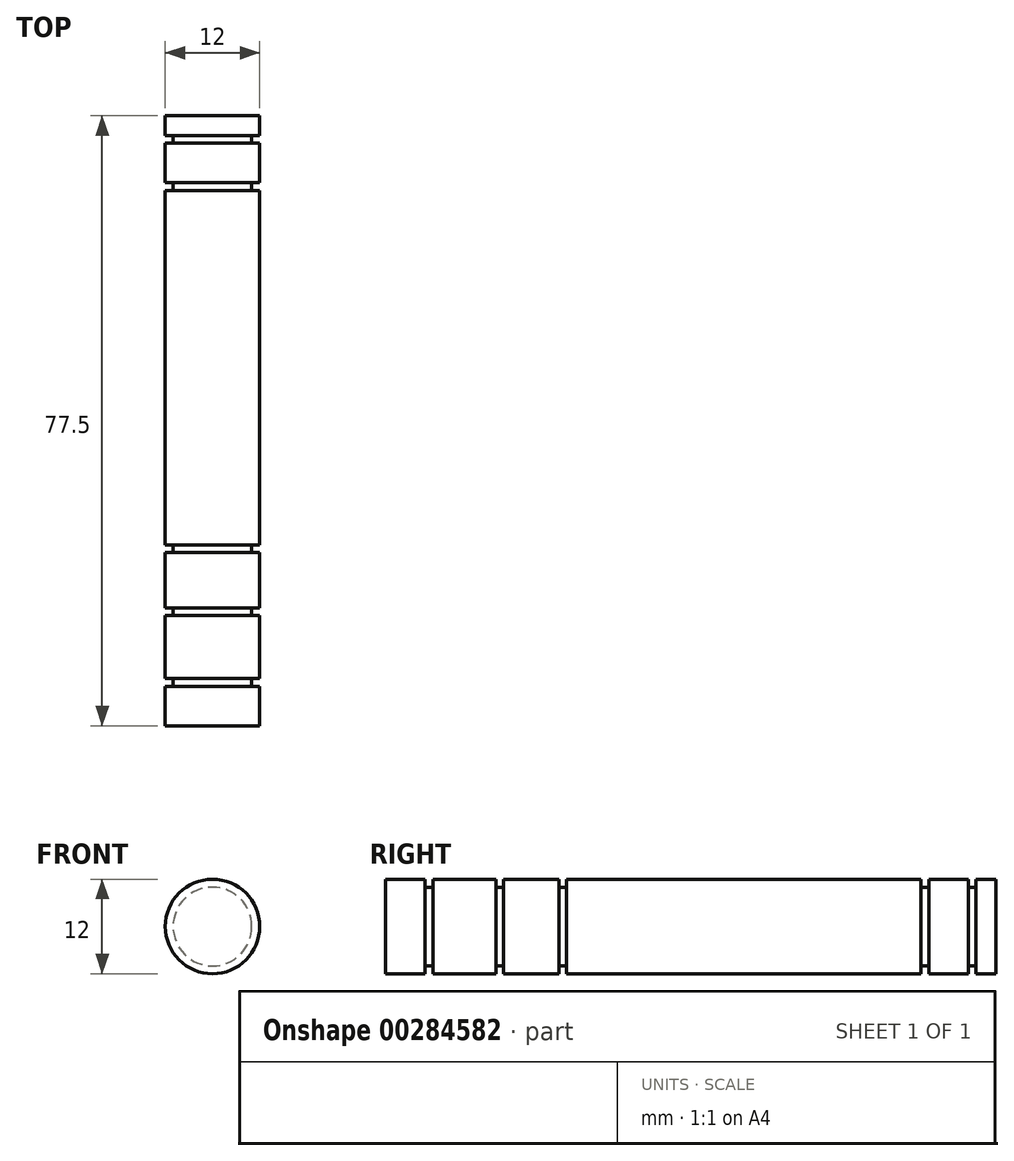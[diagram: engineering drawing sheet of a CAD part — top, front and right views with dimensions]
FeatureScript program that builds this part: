
annotation { "Feature Type Name" : "Feature", "Feature Type Description" : "" }
export const myFeature = defineFeature(function(context is Context, id is Id, definition is map)
    precondition{}
    {
        {
            var Q0;
            Q0=qCreatedBy(makeId("Right.planeOp"),FACE);
            var sketch = newSketch(context, id + "F0", { "sketchPlane" : qUnion([Q0])});
            skLineSegment(sketch, "E0.top", {"start": v(0, 6) * mm, "end": v(2, 6) * mm});
            skLineSegment(sketch, "E0.left", {"start": v(0, 0) * mm, "end": v(0, 6) * mm, "construction": true});
            skLineSegment(sketch, "E1.top", {"start": v(10, 5) * mm, "end": v(11, 5) * mm});
            skLineSegment(sketch, "E1.left", {"start": v(10, 6) * mm, "end": v(10, 5) * mm});
            skLineSegment(sketch, "E1.right", {"start": v(11, 6) * mm, "end": v(11, 5) * mm});
            skLineSegment(sketch, "E2.top", {"start": v(2, 5) * mm, "end": v(3, 5) * mm});
            skLineSegment(sketch, "E2.left", {"start": v(2, 6) * mm, "end": v(2, 5) * mm});
            skLineSegment(sketch, "E2.right", {"start": v(3, 6) * mm, "end": v(3, 5) * mm});
            skLineSegment(sketch, "E3.trimOffspring", {"start": v(3, 6) * mm, "end": v(10, 6) * mm});
            skLineSegment(sketch, "E4.trimOffspring", {"start": v(11, 6) * mm, "end": v(29, 6) * mm});
            skLineSegment(sketch, "E5.top", {"start": v(56, 5) * mm, "end": v(57, 5) * mm});
            skLineSegment(sketch, "E5.left", {"start": v(56, 6) * mm, "end": v(56, 5) * mm});
            skLineSegment(sketch, "E5.right", {"start": v(57, 6) * mm, "end": v(57, 5) * mm});
            skLineSegment(sketch, "E6", {"start": v(57, 6) * mm, "end": v(62, 6) * mm});
            skLineSegment(sketch, "E7", {"start": v(62, 6) * mm, "end": v(62, 5) * mm});
            skLineSegment(sketch, "E8", {"start": v(62, 5) * mm, "end": v(63, 5) * mm});
            skLineSegment(sketch, "E9", {"start": v(63, 5) * mm, "end": v(63, 6) * mm});
            skLineSegment(sketch, "E10", {"start": v(0, 0) * mm, "end": v(65.5, 0) * mm});
            skLineSegment(sketch, "E11.trimOffspring", {"start": v(30, 6) * mm, "end": v(56, 6) * mm});
            skLineSegment(sketch, "E12", {"start": v(2, 6) * mm, "end": v(0, 6) * mm});
            skLineSegment(sketch, "E13", {"start": v(-12, 6) * mm, "end": v(-12, 0) * mm});
            skLineSegment(sketch, "E14", {"start": v(-12, 0) * mm, "end": v(0, 0) * mm});
            skLineSegment(sketch, "E15", {"start": v(29, 6) * mm, "end": v(30, 6) * mm});
            skLineSegment(sketch, "E16", {"start": v(65.5, 0) * mm, "end": v(65.5, 6) * mm});
            skLineSegment(sketch, "E17", {"start": v(65.5, 6) * mm, "end": v(63, 6) * mm});
            skLineSegment(sketch, "E18", {"start": v(-6, 6) * mm, "end": v(-6, 5) * mm});
            skLineSegment(sketch, "E19", {"start": v(-6, 5) * mm, "end": v(-7, 5) * mm});
            skLineSegment(sketch, "E20", {"start": v(-7, 5) * mm, "end": v(-7, 6) * mm});
            skLineSegment(sketch, "E21.trimOffspring", {"start": v(-6, 6) * mm, "end": v(2, 6) * mm});
            skLineSegment(sketch, "E22.trimOffspring", {"start": v(2, 6) * mm, "end": v(-6, 6) * mm});
            skLineSegment(sketch, "E23.trimOffspring", {"start": v(-7, 6) * mm, "end": v(-12, 6) * mm});
            skSolve(sketch);
        }
        {
            var Q0;
            Q0=qSketchRegion(id+"F0",true);
            var Q1;
            Q1=sQuery(id+"F0.wireOp",EDGE,"E10");
            revolve(context, id + "F1", {"entities" : qUnion([Q0]), "axis" : qUnion([Q1]), "revolveType" : RevolveType.FULL});
        }
    });
